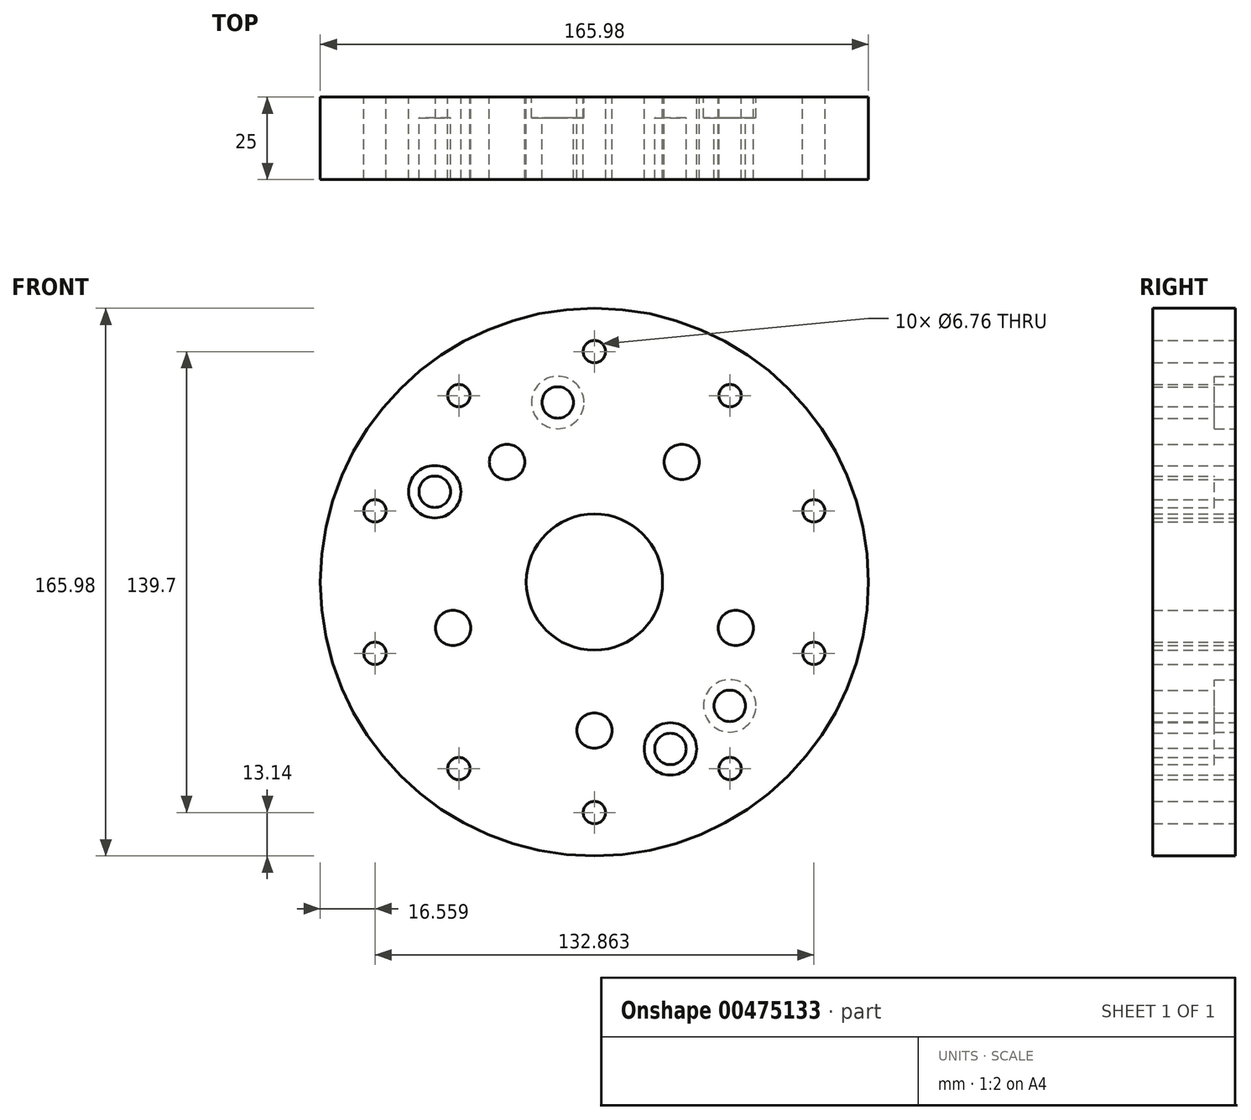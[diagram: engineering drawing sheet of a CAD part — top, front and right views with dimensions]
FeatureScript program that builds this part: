
annotation { "Feature Type Name" : "Feature", "Feature Type Description" : "" }
export const myFeature = defineFeature(function(context is Context, id is Id, definition is map)
    precondition{}
    {
        {
            var Q0;
            Q0=qCreatedBy(makeId("Front.planeOp"),FACE);
            var sketch = newSketch(context, id + "F0", { "sketchPlane" : qUnion([Q0])});
            skCircle(sketch, "E0", {"center": v(0, 0) * mm, "radius": 83 * mm});
            skCircle(sketch, "E1", {"center": v(0, 0) * mm, "radius": 20.64 * mm});
            skCircle(sketch, "E2", {"center": v(0, 0) * mm, "radius": 69.85 * mm, "construction": true});
            skLineSegment(sketch, "E3", {"start": v(-6.35, 61.72) * mm, "end": v(-6.35, 40.65) * mm, "construction": true});
            skLineSegment(sketch, "E4", {"start": v(-11.11, 61.72) * mm, "end": v(-11.11, 40.25) * mm, "construction": true});
            skCircle(sketch, "E5", {"center": v(-11.11, 54.44) * mm, "radius": 4.76 * mm});
            skLineSegment(sketch, "E6", {"start": v(0, 0) * mm, "end": v(-55.96, 77.02) * mm, "construction": true});
            skCircle(sketch, "E7.MirrorC", {"center": v(-48.34, 27.4) * mm, "radius": 4.76 * mm});
            skLineSegment(sketch, "E8.MirrorCS", {"start": v(-56.74, 25.11) * mm, "end": v(-36.7, 18.6) * mm, "construction": true});
            skPoint(sketch, "E9", {"position": v(0, 69.85) * mm});
            skPoint(sketch, "E10.1.0", {"position": v(-41.06, 56.5) * mm});
            skPoint(sketch, "E10.2.0", {"position": v(-66.43, 21.58) * mm});
            skPoint(sketch, "E10.3.0", {"position": v(-66.43, -21.58) * mm});
            skPoint(sketch, "E10.4.0", {"position": v(-41.06, -56.5) * mm});
            skPoint(sketch, "E10.5.0", {"position": v(0, -69.85) * mm});
            skPoint(sketch, "E10.6.0", {"position": v(41.06, -56.5) * mm});
            skPoint(sketch, "E10.7.0", {"position": v(66.43, -21.58) * mm});
            skPoint(sketch, "E10.8.0", {"position": v(66.43, 21.58) * mm});
            skPoint(sketch, "E10.9.0", {"position": v(41.06, 56.5) * mm});
            skCircle(sketch, "E11", {"center": v(-11.11, 54.44) * mm, "radius": 7.94 * mm});
            skCircle(sketch, "E12", {"center": v(-48.34, 27.4) * mm, "radius": 7.94 * mm});
            skCircle(sketch, "E13", {"center": v(0, 0) * mm, "radius": 60.33 * mm, "construction": true});
            skLineSegment(sketch, "E14", {"start": v(0, -69.85) * mm, "end": v(0, 0) * mm, "construction": true});
            skCircle(sketch, "E15.1.0", {"center": v(-40.99, -37.51) * mm, "radius": 4.76 * mm});
            skCircle(sketch, "E15.1.1", {"center": v(-40.99, -37.51) * mm, "radius": 7.94 * mm});
            skCircle(sketch, "E15.1.2", {"center": v(-55.2, 6.25) * mm, "radius": 7.94 * mm});
            skCircle(sketch, "E15.1.3", {"center": v(-55.2, 6.25) * mm, "radius": 4.76 * mm});
            skCircle(sketch, "E15.2.0", {"center": v(23, -50.57) * mm, "radius": 4.76 * mm});
            skCircle(sketch, "E15.2.1", {"center": v(23, -50.57) * mm, "radius": 7.94 * mm});
            skCircle(sketch, "E15.2.2", {"center": v(-23, -50.57) * mm, "radius": 7.94 * mm});
            skCircle(sketch, "E15.2.3", {"center": v(-23, -50.57) * mm, "radius": 4.76 * mm});
            skCircle(sketch, "E15.3.0", {"center": v(55.2, 6.25) * mm, "radius": 4.76 * mm});
            skCircle(sketch, "E15.3.1", {"center": v(55.2, 6.25) * mm, "radius": 7.94 * mm});
            skCircle(sketch, "E15.3.2", {"center": v(40.99, -37.51) * mm, "radius": 7.94 * mm});
            skCircle(sketch, "E15.3.3", {"center": v(40.99, -37.51) * mm, "radius": 4.76 * mm});
            skCircle(sketch, "E15.4.0", {"center": v(11.11, 54.44) * mm, "radius": 4.76 * mm});
            skCircle(sketch, "E15.4.1", {"center": v(11.11, 54.44) * mm, "radius": 7.94 * mm});
            skCircle(sketch, "E15.4.2", {"center": v(48.34, 27.4) * mm, "radius": 7.94 * mm});
            skCircle(sketch, "E15.4.3", {"center": v(48.34, 27.4) * mm, "radius": 4.76 * mm});
            skSolve(sketch);
        }
        {
            var Q0;
            Q0=makeQuery(id+"F0.imprint","IMPRINT",FACE,{"disambiguationData":[TD([[makeQuery(id+"F0.imprint","IMPRINT",EDGE,{"derivedFrom":sQuery(id+"F0.wireOp",EDGE,"E0")}),1.0]])]});
            var Q1;
            Q1=makeQuery(id+"F0.imprint","IMPRINT",FACE,{"disambiguationData":[TD([[makeQuery(id+"F0.imprint","IMPRINT",EDGE,{"derivedFrom":sQuery(id+"F0.wireOp",EDGE,"4ab3ce47-7b3f-4ca4-abf6-61af778339a8.1.1")}),1.0]])]});
            var Q2;
            Q2=makeQuery(id+"F0.imprint","IMPRINT",FACE,{"disambiguationData":[TD([[makeQuery(id+"F0.imprint","IMPRINT",EDGE,{"derivedFrom":sQuery(id+"F0.wireOp",EDGE,"4ab3ce47-7b3f-4ca4-abf6-61af778339a8.1.0")}),-1.0]])]});
            var Q3;
            Q3=makeQuery(id+"F0.imprint","IMPRINT",FACE,{"disambiguationData":[TD([[makeQuery(id+"F0.imprint","IMPRINT",EDGE,{"derivedFrom":sQuery(id+"F0.wireOp",EDGE,"E7.MirrorC")}),1.0]])]});
            var Q4;
            Q4=makeQuery(id+"F0.imprint","IMPRINT",FACE,{"disambiguationData":[TD([[makeQuery(id+"F0.imprint","IMPRINT",EDGE,{"derivedFrom":sQuery(id+"F0.wireOp",EDGE,"E5")}),-1.0]])]});
            var Q5;
            Q5=makeQuery(id+"F0.imprint","IMPRINT",FACE,{"disambiguationData":[TD([[makeQuery(id+"F0.imprint","IMPRINT",EDGE,{"derivedFrom":sQuery(id+"F0.wireOp",EDGE,"E15.1.2")}),1.0]])]});
            var Q6;
            Q6=makeQuery(id+"F0.imprint","IMPRINT",FACE,{"disambiguationData":[TD([[makeQuery(id+"F0.imprint","IMPRINT",EDGE,{"derivedFrom":sQuery(id+"F0.wireOp",EDGE,"E15.1.3")}),1.0]])]});
            var Q7;
            Q7=makeQuery(id+"F0.imprint","IMPRINT",FACE,{"disambiguationData":[TD([[makeQuery(id+"F0.imprint","IMPRINT",EDGE,{"derivedFrom":sQuery(id+"F0.wireOp",EDGE,"E15.1.0")}),-1.0]])]});
            var Q8;
            Q8=makeQuery(id+"F0.imprint","IMPRINT",FACE,{"disambiguationData":[TD([[makeQuery(id+"F0.imprint","IMPRINT",EDGE,{"derivedFrom":sQuery(id+"F0.wireOp",EDGE,"E15.1.0")}),1.0]])]});
            var Q9;
            Q9=makeQuery(id+"F0.imprint","IMPRINT",FACE,{"disambiguationData":[TD([[makeQuery(id+"F0.imprint","IMPRINT",EDGE,{"derivedFrom":sQuery(id+"F0.wireOp",EDGE,"E15.2.3")}),1.0]])]});
            var Q10;
            Q10=makeQuery(id+"F0.imprint","IMPRINT",FACE,{"disambiguationData":[TD([[makeQuery(id+"F0.imprint","IMPRINT",EDGE,{"derivedFrom":sQuery(id+"F0.wireOp",EDGE,"E15.2.2")}),1.0]])]});
            var Q11;
            Q11=makeQuery(id+"F0.imprint","IMPRINT",FACE,{"disambiguationData":[TD([[makeQuery(id+"F0.imprint","IMPRINT",EDGE,{"derivedFrom":sQuery(id+"F0.wireOp",EDGE,"E15.3.0")}),1.0]])]});
            var Q12;
            Q12=makeQuery(id+"F0.imprint","IMPRINT",FACE,{"disambiguationData":[TD([[makeQuery(id+"F0.imprint","IMPRINT",EDGE,{"derivedFrom":sQuery(id+"F0.wireOp",EDGE,"E15.3.0")}),-1.0]])]});
            var Q13;
            Q13=makeQuery(id+"F0.imprint","IMPRINT",FACE,{"disambiguationData":[TD([[makeQuery(id+"F0.imprint","IMPRINT",EDGE,{"derivedFrom":sQuery(id+"F0.wireOp",EDGE,"E15.4.2")}),1.0]])]});
            var Q14;
            Q14=makeQuery(id+"F0.imprint","IMPRINT",FACE,{"disambiguationData":[TD([[makeQuery(id+"F0.imprint","IMPRINT",EDGE,{"derivedFrom":sQuery(id+"F0.wireOp",EDGE,"E15.4.3")}),1.0]])]});
            var Q15;
            Q15=makeQuery(id+"F0.imprint","IMPRINT",FACE,{"disambiguationData":[TD([[makeQuery(id+"F0.imprint","IMPRINT",EDGE,{"derivedFrom":sQuery(id+"F0.wireOp",EDGE,"E15.4.0")}),1.0]])]});
            var Q16;
            Q16=makeQuery(id+"F0.imprint","IMPRINT",FACE,{"disambiguationData":[TD([[makeQuery(id+"F0.imprint","IMPRINT",EDGE,{"derivedFrom":sQuery(id+"F0.wireOp",EDGE,"E15.4.0")}),-1.0]])]});
            var Q17;
            Q17=makeQuery(id+"F0.imprint","IMPRINT",FACE,{"disambiguationData":[TD([[makeQuery(id+"F0.imprint","IMPRINT",EDGE,{"derivedFrom":sQuery(id+"F0.wireOp",EDGE,"E15.2.0")}),1.0]])]});
            var Q18;
            Q18=makeQuery(id+"F0.imprint","IMPRINT",FACE,{"disambiguationData":[TD([[makeQuery(id+"F0.imprint","IMPRINT",EDGE,{"derivedFrom":sQuery(id+"F0.wireOp",EDGE,"E15.3.2")}),1.0]])]});
            extrude(context, id + "F1", {"entities" : qUnion([Q0, Q1, Q2, Q3, Q4, Q5, Q6, Q7, Q8, Q9, Q10, Q11, Q12, Q13, Q14, Q15, Q16, Q17, Q18]), "depth" : 25 * mm});
        }
        {
            var Q0;
            Q0=sQuery(id+"F0.wireOp",VERTEX,"E9");
            var Q1;
            Q1=sQuery(id+"F0.wireOp",VERTEX,"E10.9.0");
            var Q2;
            Q2=sQuery(id+"F0.wireOp",VERTEX,"E10.8.0");
            var Q3;
            Q3=sQuery(id+"F0.wireOp",VERTEX,"E10.7.0");
            var Q4;
            Q4=sQuery(id+"F0.wireOp",VERTEX,"E10.6.0");
            var Q5;
            Q5=sQuery(id+"F0.wireOp",VERTEX,"E10.5.0");
            var Q6;
            Q6=sQuery(id+"F0.wireOp",VERTEX,"E10.4.0");
            var Q7;
            Q7=sQuery(id+"F0.wireOp",VERTEX,"E10.3.0");
            var Q8;
            Q8=sQuery(id+"F0.wireOp",VERTEX,"E10.2.0");
            var Q9;
            Q9=sQuery(id+"F0.wireOp",VERTEX,"E10.1.0");
            var Q10;
            Q10=makeQuery(id+"F1.opExtrude","SWEPT_BODY",BODY,{"disambiguationData":[OSD([sQuery(id+"F0.wireOp",EDGE,"E0"),sQuery(id+"F0.wireOp",EDGE,"E1"),sQuery(id+"F0.wireOp",EDGE,"E5"),sQuery(id+"F0.wireOp",EDGE,"E7.MirrorC"),sQuery(id+"F0.wireOp",EDGE,"4ab3ce47-7b3f-4ca4-abf6-61af778339a8.1.0"),sQuery(id+"F0.wireOp",EDGE,"4ab3ce47-7b3f-4ca4-abf6-61af778339a8.1.1")])]});
            hole(context, id + "F2", {"style" : HoleStyle.SIMPLE, "endStyle" : HoleEndStyle.THROUGH, "oppositeDirection" : true, "standardTappedOrClearance" : lookupTablePath({ "standard" : "ANSI", "fit" : "Normal (ASME)", "size" : "1/4", "type" : "Clearance" }), "standardBlindInLast" : lookupTablePath({ "fit" : "Free", "standard" : "ANSI", "size" : "1/4", "type" : "Clearance" }), "holeDiameter" : 6.76 * mm, "tappedDepth" : 12 * mm, "tapClearance" : 3, "startFromSketch" : true, "locations" : qUnion([Q0, Q1, Q2, Q3, Q4, Q5, Q6, Q7, Q8, Q9]), "scope" : qUnion([Q10])});
        }
        {
            var Q0;
            Q0=makeQuery(id+"F0.imprint","IMPRINT",FACE,{"disambiguationData":[TD([[makeQuery(id+"F0.imprint","IMPRINT",EDGE,{"derivedFrom":sQuery(id+"F0.wireOp",EDGE,"4ab3ce47-7b3f-4ca4-abf6-61af778339a8.1.1")}),1.0]])]});
            var Q1;
            Q1=makeQuery(id+"F0.imprint","IMPRINT",FACE,{"disambiguationData":[TD([[makeQuery(id+"F0.imprint","IMPRINT",EDGE,{"derivedFrom":sQuery(id+"F0.wireOp",EDGE,"4ab3ce47-7b3f-4ca4-abf6-61af778339a8.1.0")}),-1.0]])]});
            var Q2;
            Q2=makeQuery(id+"F0.imprint","IMPRINT",FACE,{"disambiguationData":[TD([[makeQuery(id+"F0.imprint","IMPRINT",EDGE,{"derivedFrom":sQuery(id+"F0.wireOp",EDGE,"E5")}),-1.0]])]});
            var Q3;
            Q3=makeQuery(id+"F0.imprint","IMPRINT",FACE,{"disambiguationData":[TD([[makeQuery(id+"F0.imprint","IMPRINT",EDGE,{"derivedFrom":sQuery(id+"F0.wireOp",EDGE,"E7.MirrorC")}),1.0]])]});
            var Q4;
            Q4=makeQuery(id+"F0.imprint","IMPRINT",FACE,{"disambiguationData":[TD([[makeQuery(id+"F0.imprint","IMPRINT",EDGE,{"derivedFrom":sQuery(id+"F0.wireOp",EDGE,"E15.3.2")}),1.0]])]});
            var Q5;
            Q5=makeQuery(id+"F0.imprint","IMPRINT",FACE,{"disambiguationData":[TD([[makeQuery(id+"F0.imprint","IMPRINT",EDGE,{"derivedFrom":sQuery(id+"F0.wireOp",EDGE,"E15.2.0")}),1.0]])]});
            extrude(context, id + "F3", {"entities" : qUnion([Q0, Q1, Q2, Q3, Q4, Q5]), "operationType" : NewBodyOperationType.REMOVE, "depth" : 6.35 * mm});
        }
        {
            var Q0;
            Q0=makeQuery(id+"F0.imprint","IMPRINT",FACE,{"disambiguationData":[TD([[makeQuery(id+"F0.imprint","IMPRINT",EDGE,{"derivedFrom":sQuery(id+"F0.wireOp",EDGE,"E0")}),1.0]])]});
            var sketch = newSketch(context, id + "F4", { "sketchPlane" : qUnion([Q0])});
            skCircle(sketch, "E16", {"center": v(0, 0) * mm, "radius": 45 * mm, "construction": true});
            skLineSegment(sketch, "E17", {"start": v(0, 0) * mm, "end": v(0, -45) * mm, "construction": true});
            skPoint(sketch, "E18", {"position": v(0, -45) * mm});
            skPoint(sketch, "E19.1.0", {"position": v(42.8, -13.9) * mm});
            skPoint(sketch, "E19.2.0", {"position": v(26.45, 36.4) * mm});
            skPoint(sketch, "E19.3.0", {"position": v(-26.45, 36.4) * mm});
            skPoint(sketch, "E19.4.0", {"position": v(-42.8, -13.9) * mm});
            skSolve(sketch);
        }
        {
            var Q0;
            Q0=sQuery(id+"F4.wireOp",VERTEX,"E17.end");
            var Q1;
            Q1=sQuery(id+"F4.wireOp",VERTEX,"E19.1.0");
            var Q2;
            Q2=sQuery(id+"F4.wireOp",VERTEX,"E19.2.0");
            var Q3;
            Q3=sQuery(id+"F4.wireOp",VERTEX,"E19.3.0");
            var Q4;
            Q4=sQuery(id+"F4.wireOp",VERTEX,"E19.4.0");
            var Q5;
            Q5=makeQuery(id+"F1.opExtrude","SWEPT_BODY",BODY,{"disambiguationData":[OSD([sQuery(id+"F0.wireOp",EDGE,"E0"),sQuery(id+"F0.wireOp",EDGE,"E1"),sQuery(id+"F0.wireOp",EDGE,"E5"),sQuery(id+"F0.wireOp",EDGE,"E7.MirrorC"),sQuery(id+"F0.wireOp",EDGE,"E15.2.0"),sQuery(id+"F0.wireOp",EDGE,"E15.3.3")])]});
            hole(context, id + "F5", {"style" : HoleStyle.SIMPLE, "endStyle" : HoleEndStyle.THROUGH, "oppositeDirection" : true, "standardTappedOrClearance" : lookupTablePath({ "standard" : "ANSI", "engagement" : "75%", "pitch" : "13 tpi", "size" : "1/2", "type" : "Tapped" }), "standardBlindInLast" : lookupTablePath({ "standard" : "ANSI", "engagement" : "75%", "pitch" : "13 tpi", "size" : "1/2", "type" : "Tapped" }), "holeDiameter" : 10.72 * mm, "showTappedDepth" : true, "isTappedThrough" : true, "tappedDepth" : 12 * mm, "tapClearance" : 3, "startFromSketch" : true, "locations" : qUnion([Q0, Q1, Q2, Q3, Q4]), "scope" : qUnion([Q5]), "majorDiameter" : 12.7 * mm});
        }
    });
